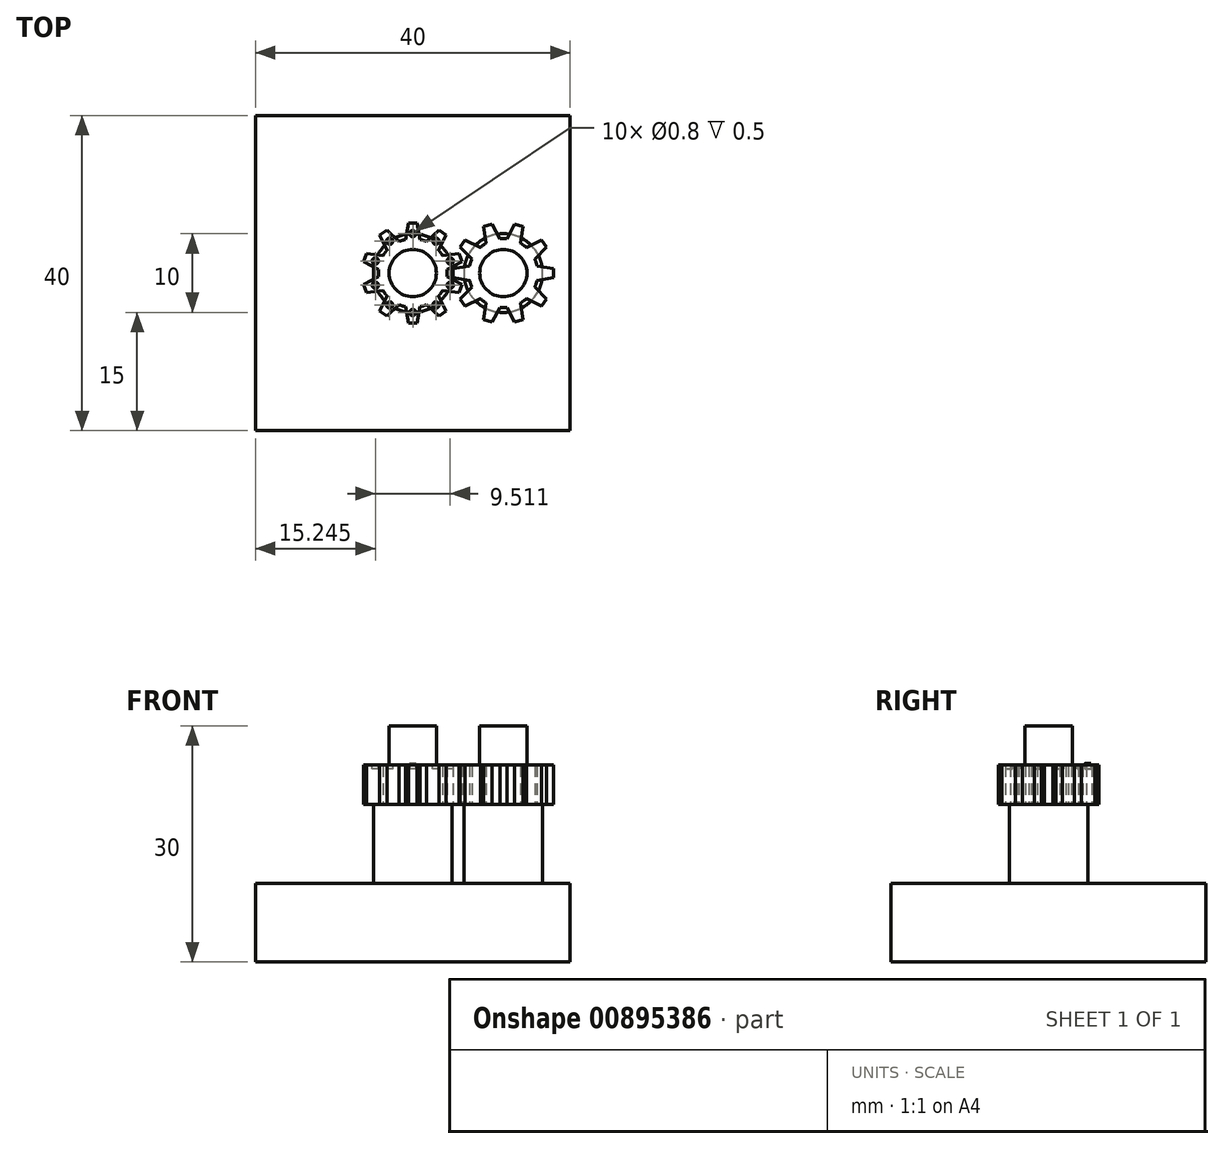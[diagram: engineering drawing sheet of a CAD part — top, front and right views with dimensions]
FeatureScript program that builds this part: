
annotation { "Feature Type Name" : "Feature", "Feature Type Description" : "" }
export const myFeature = defineFeature(function(context is Context, id is Id, definition is map)
    precondition{}
    {
        {
            var Q0;
            Q0=qCreatedBy(makeId("Top.planeOp"),FACE);
            var sketch = newSketch(context, id + "F0", { "sketchPlane" : qUnion([Q0])});
            skLineSegment(sketch, "E0.bottom", {"start": v(20, -20) * mm, "end": v(-20, -20) * mm});
            skLineSegment(sketch, "E0.top", {"start": v(20, 20) * mm, "end": v(-20, 20) * mm});
            skLineSegment(sketch, "E0.left", {"start": v(20, -20) * mm, "end": v(20, 20) * mm});
            skLineSegment(sketch, "E0.right", {"start": v(-20, -20) * mm, "end": v(-20, 20) * mm});
            skPoint(sketch, "E0.middle", {"position": v(0, 0) * mm});
            skSolve(sketch);
        }
        {
            var Q0;
            Q0 = qSketchRegion(id + "F0", true);
            extrude(context, id + "F1", {"entities" : qUnion([Q0]), "depth" : 10 * mm, "offsetDistance" : 25 * mm});
        }
        {
            var Q0;
            Q0=makeQuery(id+"F1.opExtrude","CAP_FACE",FACE,{"disambiguationData":[OSD([sQuery(id+"F0.wireOp",EDGE,"E0.bottom"),sQuery(id+"F0.wireOp",EDGE,"E0.top"),sQuery(id+"F0.wireOp",EDGE,"E0.left"),sQuery(id+"F0.wireOp",EDGE,"E0.right")])],"isStart":false});
            var sketch = newSketch(context, id + "F2", { "sketchPlane" : qUnion([Q0])});
            skCircle(sketch, "E1", {"center": v(0, 0) * mm, "radius": 5 * mm});
            skCircle(sketch, "E2", {"center": v(0, 0) * mm, "radius": 3 * mm});
            skCircle(sketch, "E3", {"center": v(11.5, 0) * mm, "radius": 5 * mm});
            skCircle(sketch, "E4", {"center": v(11.5, 0) * mm, "radius": 3 * mm});
            skSolve(sketch);
        }
        {
            var Q0;
            Q0 = qSketchRegion(id + "F2", true);
            extrude(context, id + "F3", {"entities" : qUnion([Q0]), "operationType" : NewBodyOperationType.ADD, "depth" : 10 * mm, "offsetDistance" : 25 * mm});
        }
        {
            var Q0;
            Q0=makeQuery(id+"F3.boolean.opBoolean","SPLIT",FACE,{"disambiguationData":[TD([makeQuery(id+"F3.opExtrude","SWEPT_FACE",FACE,{"disambiguationData":[OSD([sQuery(id+"F2.wireOp",EDGE,"E2")])]})])],"derivedFrom":makeQuery(id+"F1.opExtrude","CAP_FACE",FACE,{"disambiguationData":[OSD([sQuery(id+"F0.wireOp",EDGE,"E0.bottom"),sQuery(id+"F0.wireOp",EDGE,"E0.top"),sQuery(id+"F0.wireOp",EDGE,"E0.left"),sQuery(id+"F0.wireOp",EDGE,"E0.right")])],"isStart":false})});
            extrude(context, id + "F4", {"entities" : qUnion([Q0]), "depth" : 20 * mm, "offsetDistance" : 25 * mm});
        }
        {
            var Q0;
            Q0=makeQuery(id+"F3.boolean.opBoolean","SPLIT",FACE,{"disambiguationData":[TD([makeQuery(id+"F3.opExtrude","SWEPT_FACE",FACE,{"disambiguationData":[OSD([sQuery(id+"F2.wireOp",EDGE,"E4")])]})])],"derivedFrom":makeQuery(id+"F1.opExtrude","CAP_FACE",FACE,{"disambiguationData":[OSD([sQuery(id+"F0.wireOp",EDGE,"E0.bottom"),sQuery(id+"F0.wireOp",EDGE,"E0.top"),sQuery(id+"F0.wireOp",EDGE,"E0.left"),sQuery(id+"F0.wireOp",EDGE,"E0.right")])],"isStart":false})});
            extrude(context, id + "F5", {"entities" : qUnion([Q0]), "depth" : 20 * mm, "offsetDistance" : 25 * mm});
        }
        {
            var Q0;
            Q0=makeQuery(id+"F3.opExtrude","CAP_FACE",FACE,{"disambiguationData":[OSD([sQuery(id+"F2.wireOp",EDGE,"E1"),sQuery(id+"F2.wireOp",EDGE,"E2")])],"isStart":false});
            var sketch = newSketch(context, id + "F6", { "sketchPlane" : qUnion([Q0])});
            skCircle(sketch, "E5", {"center": v(0, 0) * mm, "radius": 4.38 * mm});
            skLineSegment(sketch, "E6", {"start": v(0, 6.38) * mm, "end": v(0.55, 6.38) * mm});
            skLineSegment(sketch, "E7", {"start": v(0.55, 6.38) * mm, "end": v(0.92, 4.28) * mm});
            skLineSegment(sketch, "E8.MirrorCS", {"start": v(0, 6.38) * mm, "end": v(-0.55, 6.38) * mm});
            skLineSegment(sketch, "E9.MirrorCS", {"start": v(-0.55, 6.38) * mm, "end": v(-0.92, 4.28) * mm});
            skLineSegment(sketch, "E10.1.0", {"start": v(-4.2, 4.83) * mm, "end": v(-3.26, 2.92) * mm});
            skLineSegment(sketch, "E10.1.1", {"start": v(-3.75, 5.16) * mm, "end": v(-4.2, 4.83) * mm});
            skLineSegment(sketch, "E10.1.2", {"start": v(-3.75, 5.16) * mm, "end": v(-3.3, 5.48) * mm});
            skLineSegment(sketch, "E10.1.3", {"start": v(-3.3, 5.48) * mm, "end": v(-1.77, 4) * mm});
            skLineSegment(sketch, "E10.2.0", {"start": v(-6.23, 1.45) * mm, "end": v(-4.35, 0.45) * mm});
            skLineSegment(sketch, "E10.2.1", {"start": v(-6.06, 1.97) * mm, "end": v(-6.23, 1.45) * mm});
            skLineSegment(sketch, "E10.2.2", {"start": v(-6.06, 1.97) * mm, "end": v(-5.9, 2.5) * mm});
            skLineSegment(sketch, "E10.2.3", {"start": v(-5.9, 2.5) * mm, "end": v(-3.78, 2.2) * mm});
            skLineSegment(sketch, "E10.3.0", {"start": v(-5.9, -2.5) * mm, "end": v(-3.78, -2.2) * mm});
            skLineSegment(sketch, "E10.3.1", {"start": v(-6.06, -1.97) * mm, "end": v(-5.9, -2.5) * mm});
            skLineSegment(sketch, "E10.3.2", {"start": v(-6.06, -1.97) * mm, "end": v(-6.23, -1.45) * mm});
            skLineSegment(sketch, "E10.3.3", {"start": v(-6.23, -1.45) * mm, "end": v(-4.35, -0.45) * mm});
            skLineSegment(sketch, "E10.4.0", {"start": v(-3.3, -5.48) * mm, "end": v(-1.77, -4) * mm});
            skLineSegment(sketch, "E10.4.1", {"start": v(-3.75, -5.16) * mm, "end": v(-3.3, -5.48) * mm});
            skLineSegment(sketch, "E10.4.2", {"start": v(-3.75, -5.16) * mm, "end": v(-4.2, -4.83) * mm});
            skLineSegment(sketch, "E10.4.3", {"start": v(-4.2, -4.83) * mm, "end": v(-3.26, -2.92) * mm});
            skLineSegment(sketch, "E10.5.0", {"start": v(0.55, -6.38) * mm, "end": v(0.92, -4.28) * mm});
            skLineSegment(sketch, "E10.5.1", {"start": v(0, -6.38) * mm, "end": v(0.55, -6.38) * mm});
            skLineSegment(sketch, "E10.5.2", {"start": v(0, -6.38) * mm, "end": v(-0.55, -6.38) * mm});
            skLineSegment(sketch, "E10.5.3", {"start": v(-0.55, -6.38) * mm, "end": v(-0.92, -4.28) * mm});
            skLineSegment(sketch, "E10.6.0", {"start": v(4.2, -4.83) * mm, "end": v(3.26, -2.92) * mm});
            skLineSegment(sketch, "E10.6.1", {"start": v(3.75, -5.16) * mm, "end": v(4.2, -4.83) * mm});
            skLineSegment(sketch, "E10.6.2", {"start": v(3.75, -5.16) * mm, "end": v(3.3, -5.48) * mm});
            skLineSegment(sketch, "E10.6.3", {"start": v(3.3, -5.48) * mm, "end": v(1.77, -4) * mm});
            skLineSegment(sketch, "E10.7.0", {"start": v(6.23, -1.45) * mm, "end": v(4.35, -0.45) * mm});
            skLineSegment(sketch, "E10.7.1", {"start": v(6.06, -1.97) * mm, "end": v(6.23, -1.45) * mm});
            skLineSegment(sketch, "E10.7.2", {"start": v(6.06, -1.97) * mm, "end": v(5.9, -2.5) * mm});
            skLineSegment(sketch, "E10.7.3", {"start": v(5.9, -2.5) * mm, "end": v(3.78, -2.2) * mm});
            skLineSegment(sketch, "E10.8.0", {"start": v(5.9, 2.5) * mm, "end": v(3.78, 2.2) * mm});
            skLineSegment(sketch, "E10.8.1", {"start": v(6.06, 1.97) * mm, "end": v(5.9, 2.5) * mm});
            skLineSegment(sketch, "E10.8.2", {"start": v(6.06, 1.97) * mm, "end": v(6.23, 1.45) * mm});
            skLineSegment(sketch, "E10.8.3", {"start": v(6.23, 1.45) * mm, "end": v(4.35, 0.45) * mm});
            skLineSegment(sketch, "E10.9.0", {"start": v(3.3, 5.48) * mm, "end": v(1.77, 4) * mm});
            skLineSegment(sketch, "E10.9.1", {"start": v(3.75, 5.16) * mm, "end": v(3.3, 5.48) * mm});
            skLineSegment(sketch, "E10.9.2", {"start": v(3.75, 5.16) * mm, "end": v(4.2, 4.83) * mm});
            skLineSegment(sketch, "E10.9.3", {"start": v(4.2, 4.83) * mm, "end": v(3.26, 2.92) * mm});
            skSolve(sketch);
        }
        {
            var Q0;
            Q0 = qSketchRegion(id + "F6", true);
            extrude(context, id + "F7", {"entities" : qUnion([Q0]), "operationType" : NewBodyOperationType.ADD, "depth" : 5 * mm, "offsetDistance" : 25 * mm});
        }
        {
            var Q0;
            Q0=makeQuery(id+"F3.opExtrude","CAP_FACE",FACE,{"disambiguationData":[OSD([sQuery(id+"F2.wireOp",EDGE,"E3"),sQuery(id+"F2.wireOp",EDGE,"E4")])],"isStart":false});
            var sketch = newSketch(context, id + "F8", { "sketchPlane" : qUnion([Q0])});
            skCircle(sketch, "E11", {"center": v(11.5, 0) * mm, "radius": 4.38 * mm});
            skLineSegment(sketch, "E12", {"start": v(5.12, 0) * mm, "end": v(5.12, 0.55) * mm});
            skLineSegment(sketch, "E13", {"start": v(5.12, 0.55) * mm, "end": v(7.22, 0.92) * mm});
            skLineSegment(sketch, "E14.MirrorCS", {"start": v(5.12, 0) * mm, "end": v(5.12, -0.55) * mm});
            skLineSegment(sketch, "E15.MirrorCS", {"start": v(5.12, -0.55) * mm, "end": v(7.22, -0.92) * mm});
            skLineSegment(sketch, "E16.1.0", {"start": v(6.67, -4.2) * mm, "end": v(8.58, -3.26) * mm});
            skLineSegment(sketch, "E16.1.1", {"start": v(6.34, -3.75) * mm, "end": v(6.67, -4.2) * mm});
            skLineSegment(sketch, "E16.1.2", {"start": v(6.34, -3.75) * mm, "end": v(6.02, -3.3) * mm});
            skLineSegment(sketch, "E16.1.3", {"start": v(6.02, -3.3) * mm, "end": v(7.5, -1.77) * mm});
            skLineSegment(sketch, "E16.2.0", {"start": v(10.05, -6.23) * mm, "end": v(11.05, -4.35) * mm});
            skLineSegment(sketch, "E16.2.1", {"start": v(9.53, -6.06) * mm, "end": v(10.05, -6.23) * mm});
            skLineSegment(sketch, "E16.2.2", {"start": v(9.53, -6.06) * mm, "end": v(9, -5.9) * mm});
            skLineSegment(sketch, "E16.2.3", {"start": v(9, -5.9) * mm, "end": v(9.3, -3.78) * mm});
            skLineSegment(sketch, "E17.1.3.0", {"start": v(14, -5.9) * mm, "end": v(13.7, -3.78) * mm});
            skLineSegment(sketch, "E17.3.3.0", {"start": v(13.47, -6.06) * mm, "end": v(14, -5.9) * mm});
            skLineSegment(sketch, "E17.6.3.0", {"start": v(13.47, -6.06) * mm, "end": v(12.95, -6.23) * mm});
            skLineSegment(sketch, "E17.9.3.0", {"start": v(12.95, -6.23) * mm, "end": v(11.95, -4.35) * mm});
            skLineSegment(sketch, "E17.1.4.0", {"start": v(16.98, -3.3) * mm, "end": v(15.5, -1.77) * mm});
            skLineSegment(sketch, "E17.3.4.0", {"start": v(16.66, -3.75) * mm, "end": v(16.98, -3.3) * mm});
            skLineSegment(sketch, "E17.6.4.0", {"start": v(16.66, -3.75) * mm, "end": v(16.33, -4.2) * mm});
            skLineSegment(sketch, "E17.9.4.0", {"start": v(16.33, -4.2) * mm, "end": v(14.42, -3.26) * mm});
            skLineSegment(sketch, "E17.1.5.0", {"start": v(17.87, 0.55) * mm, "end": v(15.78, 0.92) * mm});
            skLineSegment(sketch, "E17.3.5.0", {"start": v(17.88, 0) * mm, "end": v(17.88, 0.55) * mm});
            skLineSegment(sketch, "E17.6.5.0", {"start": v(17.88, 0) * mm, "end": v(17.88, -0.55) * mm});
            skLineSegment(sketch, "E17.9.5.0", {"start": v(17.88, -0.55) * mm, "end": v(15.78, -0.92) * mm});
            skLineSegment(sketch, "E17.1.6.0", {"start": v(16.33, 4.2) * mm, "end": v(14.42, 3.26) * mm});
            skLineSegment(sketch, "E17.3.6.0", {"start": v(16.66, 3.75) * mm, "end": v(16.33, 4.2) * mm});
            skLineSegment(sketch, "E17.6.6.0", {"start": v(16.66, 3.75) * mm, "end": v(16.98, 3.3) * mm});
            skLineSegment(sketch, "E17.9.6.0", {"start": v(16.98, 3.3) * mm, "end": v(15.5, 1.77) * mm});
            skLineSegment(sketch, "E17.1.7.0", {"start": v(12.95, 6.23) * mm, "end": v(11.95, 4.35) * mm});
            skLineSegment(sketch, "E17.3.7.0", {"start": v(13.47, 6.06) * mm, "end": v(12.95, 6.23) * mm});
            skLineSegment(sketch, "E17.6.7.0", {"start": v(13.47, 6.06) * mm, "end": v(14, 5.9) * mm});
            skLineSegment(sketch, "E17.9.7.0", {"start": v(14, 5.9) * mm, "end": v(13.7, 3.78) * mm});
            skLineSegment(sketch, "E17.1.8.0", {"start": v(9, 5.9) * mm, "end": v(9.3, 3.78) * mm});
            skLineSegment(sketch, "E17.3.8.0", {"start": v(9.53, 6.06) * mm, "end": v(9, 5.9) * mm});
            skLineSegment(sketch, "E17.6.8.0", {"start": v(9.53, 6.06) * mm, "end": v(10.05, 6.23) * mm});
            skLineSegment(sketch, "E17.9.8.0", {"start": v(10.05, 6.23) * mm, "end": v(11.05, 4.35) * mm});
            skLineSegment(sketch, "E17.1.9.0", {"start": v(6.02, 3.3) * mm, "end": v(7.5, 1.77) * mm});
            skLineSegment(sketch, "E17.3.9.0", {"start": v(6.34, 3.75) * mm, "end": v(6.02, 3.3) * mm});
            skLineSegment(sketch, "E17.6.9.0", {"start": v(6.34, 3.75) * mm, "end": v(6.67, 4.2) * mm});
            skLineSegment(sketch, "E17.9.9.0", {"start": v(6.67, 4.2) * mm, "end": v(8.58, 3.26) * mm});
            skSolve(sketch);
        }
        {
            var Q0;
            Q0 = qSketchRegion(id + "F8", true);
            extrude(context, id + "F9", {"entities" : qUnion([Q0]), "operationType" : NewBodyOperationType.ADD, "depth" : 5 * mm, "offsetDistance" : 25 * mm});
        }
        {
            var Q0;
            Q0=makeQuery(id+"F7.opExtrude","CAP_FACE",FACE,{"disambiguationData":[OSD([sQuery(id+"F6.wireOp",EDGE,"E5"),sQuery(id+"F6.wireOp",EDGE,"E6"),sQuery(id+"F6.wireOp",EDGE,"E7"),sQuery(id+"F6.wireOp",EDGE,"E8.MirrorCS"),sQuery(id+"F6.wireOp",EDGE,"E9.MirrorCS"),sQuery(id+"F6.wireOp",EDGE,"E10.1.0"),sQuery(id+"F6.wireOp",EDGE,"E10.1.1"),sQuery(id+"F6.wireOp",EDGE,"E10.1.2"),sQuery(id+"F6.wireOp",EDGE,"E10.1.3"),sQuery(id+"F6.wireOp",EDGE,"E10.2.0"),sQuery(id+"F6.wireOp",EDGE,"E10.2.1"),sQuery(id+"F6.wireOp",EDGE,"E10.2.2"),sQuery(id+"F6.wireOp",EDGE,"E10.2.3"),sQuery(id+"F6.wireOp",EDGE,"E10.3.0"),sQuery(id+"F6.wireOp",EDGE,"E10.3.1"),sQuery(id+"F6.wireOp",EDGE,"E10.3.2"),sQuery(id+"F6.wireOp",EDGE,"E10.3.3"),sQuery(id+"F6.wireOp",EDGE,"E10.4.0"),sQuery(id+"F6.wireOp",EDGE,"E10.4.1"),sQuery(id+"F6.wireOp",EDGE,"E10.4.2"),sQuery(id+"F6.wireOp",EDGE,"E10.4.3"),sQuery(id+"F6.wireOp",EDGE,"E10.5.0"),sQuery(id+"F6.wireOp",EDGE,"E10.5.1"),sQuery(id+"F6.wireOp",EDGE,"E10.5.2"),sQuery(id+"F6.wireOp",EDGE,"E10.5.3"),sQuery(id+"F6.wireOp",EDGE,"E10.6.0"),sQuery(id+"F6.wireOp",EDGE,"E10.6.1"),sQuery(id+"F6.wireOp",EDGE,"E10.6.2"),sQuery(id+"F6.wireOp",EDGE,"E10.6.3"),sQuery(id+"F6.wireOp",EDGE,"E10.7.0"),sQuery(id+"F6.wireOp",EDGE,"E10.7.1"),sQuery(id+"F6.wireOp",EDGE,"E10.7.2"),sQuery(id+"F6.wireOp",EDGE,"E10.7.3"),sQuery(id+"F6.wireOp",EDGE,"E10.8.0"),sQuery(id+"F6.wireOp",EDGE,"E10.8.1"),sQuery(id+"F6.wireOp",EDGE,"E10.8.2"),sQuery(id+"F6.wireOp",EDGE,"E10.8.3"),sQuery(id+"F6.wireOp",EDGE,"E10.9.0"),sQuery(id+"F6.wireOp",EDGE,"E10.9.1"),sQuery(id+"F6.wireOp",EDGE,"E10.9.2"),sQuery(id+"F6.wireOp",EDGE,"E10.9.3")])],"isStart":false});
            var sketch = newSketch(context, id + "F10", { "sketchPlane" : qUnion([Q0])});
            skCircle(sketch, "E18", {"center": v(0, 5) * mm, "radius": 0.4 * mm});
            skCircle(sketch, "E19.1.0", {"center": v(-2.94, 4.05) * mm, "radius": 0.4 * mm});
            skCircle(sketch, "E19.2.0", {"center": v(-4.76, 1.55) * mm, "radius": 0.4 * mm});
            skPoint(sketch, "E19.center", {"position": v(0, 0) * mm});
            skCircle(sketch, "E20.1.3.0", {"center": v(-4.76, -1.55) * mm, "radius": 0.4 * mm});
            skCircle(sketch, "E20.1.4.0", {"center": v(-2.94, -4.05) * mm, "radius": 0.4 * mm});
            skCircle(sketch, "E20.1.5.0", {"center": v(0, -5) * mm, "radius": 0.4 * mm});
            skCircle(sketch, "E20.1.6.0", {"center": v(2.94, -4.05) * mm, "radius": 0.4 * mm});
            skCircle(sketch, "E20.1.7.0", {"center": v(4.76, -1.55) * mm, "radius": 0.4 * mm});
            skCircle(sketch, "E20.1.8.0", {"center": v(4.76, 1.55) * mm, "radius": 0.4 * mm});
            skCircle(sketch, "E20.1.9.0", {"center": v(2.94, 4.05) * mm, "radius": 0.4 * mm});
            skSolve(sketch);
        }
        {
            var Q0;
            Q0 = qSketchRegion(id + "F10", true);
            extrude(context, id + "F11", {"entities" : qUnion([Q0]), "operationType" : NewBodyOperationType.REMOVE, "oppositeDirection" : true, "depth" : 0.5 * mm, "offsetDistance" : 25 * mm});
        }
        {
            var Q0;
            Q0=makeQuery(id+"F11.boolean.opBoolean","COPY",FACE,{"derivedFrom":makeQuery(id+"F11.opExtrude","CAP_FACE",FACE,{"disambiguationData":[OSD([sQuery(id+"F10.wireOp",EDGE,"E18")])],"isStart":false})});
            extrude(context, id + "F12", {"entities" : qUnion([Q0]), "depth" : 0.7 * mm, "offsetDistance" : 25 * mm});
        }
    });
